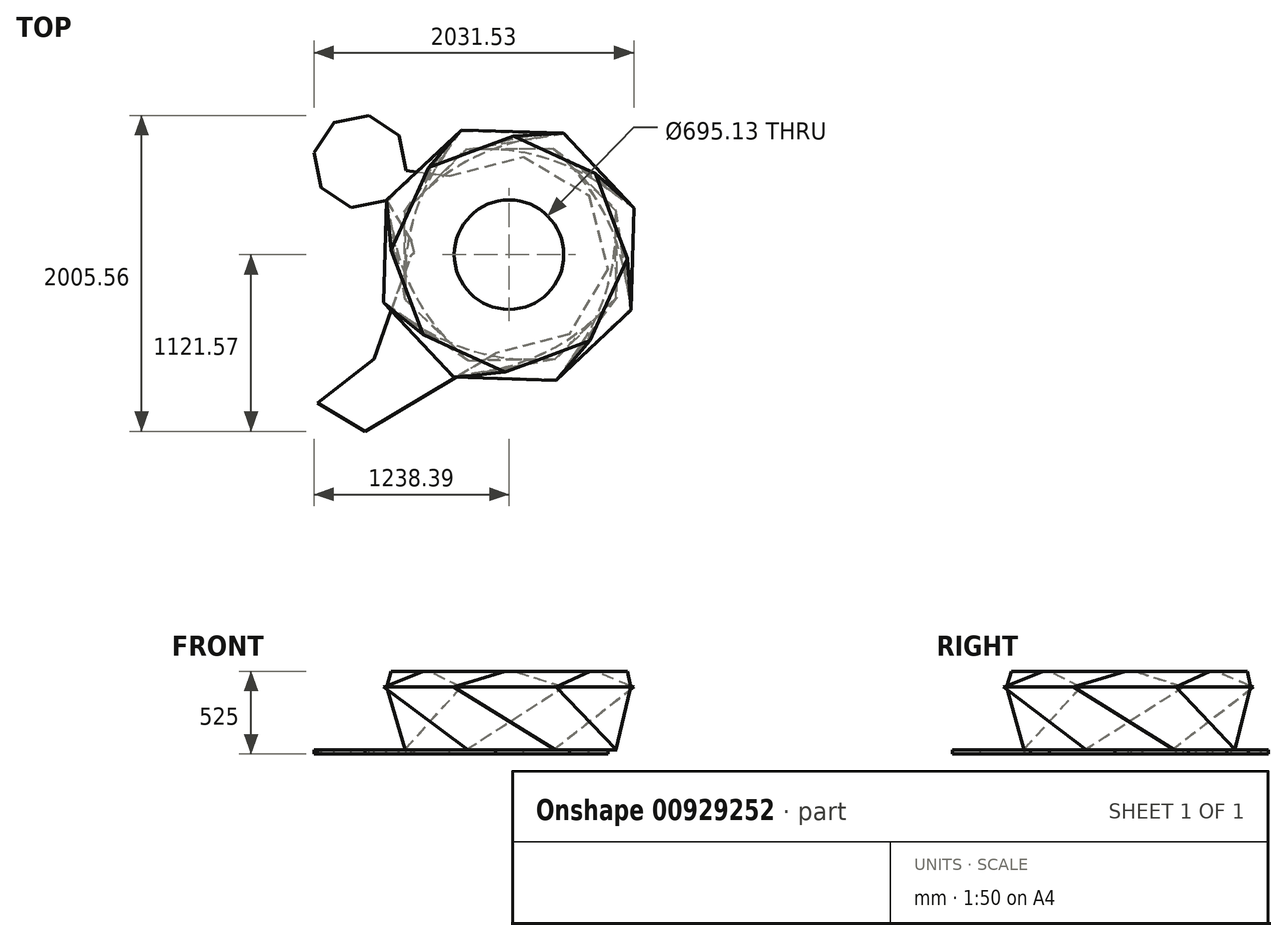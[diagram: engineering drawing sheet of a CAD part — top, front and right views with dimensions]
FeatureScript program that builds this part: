
annotation { "Feature Type Name" : "Feature", "Feature Type Description" : "" }
export const myFeature = defineFeature(function(context is Context, id is Id, definition is map)
    precondition{}
    {
        {
            var Q0;
            Q0=qCreatedBy(makeId("Top.planeOp"),FACE);
            var sketch = newSketch(context, id + "F0", { "sketchPlane" : qUnion([Q0])});
            skLineSegment(sketch, "E0", {"start": v(0, 0) * mm, "end": v(-1250, 0) * mm, "construction": true});
            skLineSegment(sketch, "E1", {"start": v(0, 0) * mm, "end": v(0, 1250) * mm, "construction": true});
            skLineSegment(sketch, "E2", {"start": v(0, 1250) * mm, "end": v(-1250, 0) * mm, "construction": true});
            skLineSegment(sketch, "E3.bottom", {"start": v(-1250, 0) * mm, "end": v(0, 0) * mm, "construction": true});
            skLineSegment(sketch, "E3.top", {"start": v(-1250, 1250) * mm, "end": v(0, 1250) * mm, "construction": true});
            skLineSegment(sketch, "E3.left", {"start": v(-1250, 0) * mm, "end": v(-1250, 1250) * mm, "construction": true});
            skLineSegment(sketch, "E4", {"start": v(-1250, 1250) * mm, "end": v(0, 0) * mm, "construction": true});
            skLineSegment(sketch, "E5", {"start": v(-625, 625) * mm, "end": v(0, 625) * mm, "construction": true});
            skLineSegment(sketch, "E6", {"start": v(0, 625) * mm, "end": v(-625, 625) * mm, "construction": true});
            skLineSegment(sketch, "E7", {"start": v(-625, 625) * mm, "end": v(-1250, 625) * mm, "construction": true});
            skLineSegment(sketch, "E8", {"start": v(-1250, 625) * mm, "end": v(-625, 625) * mm, "construction": true});
            skLineSegment(sketch, "E9", {"start": v(-625, 625) * mm, "end": v(-625, 1250) * mm, "construction": true});
            skLineSegment(sketch, "E10", {"start": v(-625, 625) * mm, "end": v(-625, 0) * mm, "construction": true});
            skCircle(sketch, "E11.cCircle", {"center": v(-625, 625) * mm, "radius": 583.1 * mm, "construction": true});
            skLineSegment(sketch, "E11.0", {"start": v(-1250, 712.8) * mm, "end": v(-1004.86, 1129.03) * mm});
            skLineSegment(sketch, "E11.1", {"start": v(-1004.86, 1129.03) * mm, "end": v(-537.2, 1250) * mm});
            skLineSegment(sketch, "E11.2", {"start": v(-537.2, 1250) * mm, "end": v(-120.97, 1004.86) * mm});
            skLineSegment(sketch, "E11.3", {"start": v(-120.97, 1004.86) * mm, "end": v(0, 537.2) * mm});
            skLineSegment(sketch, "E11.4", {"start": v(0, 537.2) * mm, "end": v(-245.14, 120.97) * mm});
            skLineSegment(sketch, "E11.5", {"start": v(-245.14, 120.97) * mm, "end": v(-712.8, 0) * mm});
            skLineSegment(sketch, "E11.6", {"start": v(-712.8, 0) * mm, "end": v(-1129.03, 245.14) * mm});
            skLineSegment(sketch, "E11.7", {"start": v(-1129.03, 245.14) * mm, "end": v(-1250, 712.8) * mm});
            skPoint(sketch, "E11.0.midPoint", {"position": v(-1127.43, 920.91) * mm});
            skLineSegment(sketch, "E12", {"start": v(-1127.43, 920.91) * mm, "end": v(-1574.38, 1218.8) * mm, "construction": true});
            skCircle(sketch, "E13.cCircle", {"center": v(-1574.38, 1218.8) * mm, "radius": 275.36 * mm, "construction": true});
            skLineSegment(sketch, "E13.0", {"start": v(-1632.18, 926.4) * mm, "end": v(-1822, 1052.9) * mm});
            skLineSegment(sketch, "E13.1", {"start": v(-1822, 1052.9) * mm, "end": v(-1866.78, 1276.6) * mm});
            skLineSegment(sketch, "E13.2", {"start": v(-1866.78, 1276.6) * mm, "end": v(-1740.27, 1466.42) * mm});
            skLineSegment(sketch, "E13.3", {"start": v(-1740.27, 1466.42) * mm, "end": v(-1516.58, 1511.19) * mm});
            skLineSegment(sketch, "E13.4", {"start": v(-1516.58, 1511.19) * mm, "end": v(-1326.76, 1384.67) * mm});
            skLineSegment(sketch, "E13.5", {"start": v(-1326.76, 1384.67) * mm, "end": v(-1281.99, 1161) * mm});
            skLineSegment(sketch, "E13.6", {"start": v(-1281.99, 1161) * mm, "end": v(-1408.5, 971.17) * mm});
            skLineSegment(sketch, "E13.7", {"start": v(-1408.5, 971.17) * mm, "end": v(-1632.18, 926.4) * mm});
            skPoint(sketch, "E13.0.midPoint", {"position": v(-1727.1, 989.65) * mm});
            skLineSegment(sketch, "E14", {"start": v(-1408.5, 971.17) * mm, "end": v(-1250, 712.8) * mm});
            skLineSegment(sketch, "E15", {"start": v(-1281.99, 1161) * mm, "end": v(-1004.86, 1129.03) * mm});
            skLineSegment(sketch, "E16", {"start": v(-1129.03, 245.14) * mm, "end": v(-1845.08, -315.8) * mm});
            skLineSegment(sketch, "E17", {"start": v(-1845.08, -315.8) * mm, "end": v(-1541.9, -494.37) * mm});
            skLineSegment(sketch, "E18", {"start": v(-1541.9, -494.37) * mm, "end": v(-712.8, 0) * mm});
            skLineSegment(sketch, "E19", {"start": v(-1487.05, -35.33) * mm, "end": v(-1250, 625) * mm});
            skLineSegment(sketch, "E20", {"start": v(-1250, 625) * mm, "end": v(-1231.96, 643.04) * mm});
            skSolve(sketch);
        }
        {
            var Q0;
            Q0=makeQuery(id+"F0.imprint","IMPRINT",FACE,{"disambiguationData":[TD([[makeQuery(id+"F0.imprint","IMPRINT",EDGE,{"derivedFrom":sQuery(id+"F0.wireOp",EDGE,"E13.0")}),-1.0]])]});
            var Q1;
            Q1=makeQuery(id+"F0.imprint","IMPRINT",FACE,{"disambiguationData":[TD([[makeQuery(id+"F0.imprint","IMPRINT",EDGE,{"derivedFrom":sQuery(id+"F0.wireOp",EDGE,"E11.0")}),1.0]])]});
            var Q2;
            {var subQ0=sQuery(id+"F0.wireOp",EDGE,"E11.0");Q2=makeQuery(id+"F0.imprint","IMPRINT",FACE,{"disambiguationData":[TD([[makeQuery(id+"F0.imprint","IMPRINT",EDGE,{"derivedFrom":subQ0}),-1.0]])]});}
            var Q3;
            {var subQ4=sQuery(id+"F0.wireOp",EDGE,"E19");Q3=makeQuery(id+"F0.imprint","IMPRINT",FACE,{"disambiguationData":[TD([[makeQuery(id+"F0.imprint","IMPRINT",EDGE,{"derivedFrom":subQ4}),-1.0]])]});}
            var Q4;
            {var subQ3=sQuery(id+"F0.wireOp",EDGE,"E11.6");Q4=makeQuery(id+"F0.imprint","IMPRINT",FACE,{"disambiguationData":[TD([[makeQuery(id+"F0.imprint","IMPRINT",EDGE,{"derivedFrom":subQ3}),1.0]])]});}
            extrude(context, id + "F1", {"entities" : qUnion([Q0, Q1, Q2, Q3, Q4]), "oppositeDirection" : true, "depth" : 25 * mm, "offsetDistance" : 25 * mm});
        }
        {
            var Q0;
            Q0=qCreatedBy(makeId("Top.planeOp"),FACE);
            cPlane(context, id + "F2", {"entities" : qUnion([Q0]), "cplaneType" : CPlaneType.OFFSET, "offset" : 100 * mm, "width" : 150 * mm, "height" : 150 * mm});
        }
        {
            var Q0;
            Q0=qCreatedBy(makeId("Top.planeOp"),FACE);
            var sketch = newSketch(context, id + "F3", { "sketchPlane" : qUnion([Q0])});
            skCircle(sketch, "E21.cCircle", {"center": v(-619.06, 628.41) * mm, "radius": 671.72 * mm, "construction": true});
            skLineSegment(sketch, "E21.0", {"start": v(-1294.06, 898.6) * mm, "end": v(-905.3, 1296.76) * mm});
            skLineSegment(sketch, "E21.1", {"start": v(-905.3, 1296.76) * mm, "end": v(-348.87, 1303.41) * mm});
            skLineSegment(sketch, "E21.2", {"start": v(-348.87, 1303.41) * mm, "end": v(49.29, 914.66) * mm});
            skLineSegment(sketch, "E21.3", {"start": v(49.29, 914.66) * mm, "end": v(55.94, 358.22) * mm});
            skLineSegment(sketch, "E21.4", {"start": v(55.94, 358.22) * mm, "end": v(-332.82, -39.94) * mm});
            skLineSegment(sketch, "E21.5", {"start": v(-332.82, -39.94) * mm, "end": v(-889.25, -46.59) * mm});
            skLineSegment(sketch, "E21.6", {"start": v(-889.25, -46.59) * mm, "end": v(-1287.41, 342.17) * mm});
            skLineSegment(sketch, "E21.7", {"start": v(-1287.41, 342.17) * mm, "end": v(-1294.06, 898.6) * mm});
            skPoint(sketch, "E21.0.midPoint", {"position": v(-1099.68, 1097.68) * mm});
            skSolve(sketch);
        }
        {
            var Q0;
            Q0=qCreatedBy(makeId("Top.planeOp"),FACE);
            cPlane(context, id + "F4", {"entities" : qUnion([Q0]), "cplaneType" : CPlaneType.OFFSET, "offset" : 200 * mm, "width" : 150 * mm, "height" : 150 * mm});
        }
        {
            var Q0;
            Q0=qCreatedBy(makeId("Top.planeOp"),FACE);
            cPlane(context, id + "F5", {"entities" : qUnion([Q0]), "cplaneType" : CPlaneType.OFFSET, "offset" : 400 * mm, "width" : 150 * mm, "height" : 150 * mm});
        }
        {
            var Q0;
            Q0=qCreatedBy(id+"F5.planeOp",FACE);
            var sketch = newSketch(context, id + "F6", { "sketchPlane" : qUnion([Q0])});
            skCircle(sketch, "E22.cCircle", {"center": v(-630.1, 623.79) * mm, "radius": 785.3 * mm, "construction": true});
            skLineSegment(sketch, "E22.0", {"start": v(-1424.97, 322.63) * mm, "end": v(-1405.1, 972.9) * mm});
            skLineSegment(sketch, "E22.1", {"start": v(-1405.1, 972.9) * mm, "end": v(-931.26, 1418.65) * mm});
            skLineSegment(sketch, "E22.2", {"start": v(-931.26, 1418.65) * mm, "end": v(-281, 1398.79) * mm});
            skLineSegment(sketch, "E22.3", {"start": v(-281, 1398.79) * mm, "end": v(164.75, 924.94) * mm});
            skLineSegment(sketch, "E22.4", {"start": v(164.75, 924.94) * mm, "end": v(144.9, 274.68) * mm});
            skLineSegment(sketch, "E22.5", {"start": v(144.9, 274.68) * mm, "end": v(-328.96, -171.08) * mm});
            skLineSegment(sketch, "E22.6", {"start": v(-328.96, -171.08) * mm, "end": v(-979.22, -151.21) * mm});
            skLineSegment(sketch, "E22.7", {"start": v(-979.22, -151.21) * mm, "end": v(-1424.97, 322.63) * mm});
            skPoint(sketch, "E22.0.midPoint", {"position": v(-1415.04, 647.76) * mm});
            skSolve(sketch);
        }
        {
            var Q0;
            Q0=qCreatedBy(id+"F5.planeOp",FACE);
            cPlane(context, id + "F7", {"entities" : qUnion([Q0]), "cplaneType" : CPlaneType.OFFSET, "offset" : 100 * mm, "width" : 150 * mm, "height" : 150 * mm});
        }
        {
            var Q0;
            Q0=qCreatedBy(id+"F7.planeOp",FACE);
            var sketch = newSketch(context, id + "F8", { "sketchPlane" : qUnion([Q0])});
            skPoint(sketch, "E23.0.midPoint", {"position": v(-1069.33, 0) * mm});
            skCircle(sketch, "E24.cCircle", {"center": v(-626.9, 630.44) * mm, "radius": 692.9 * mm, "construction": true});
            skLineSegment(sketch, "E24.0", {"start": v(-653.28, -119.1) * mm, "end": v(-1175.56, 119.1) * mm});
            skLineSegment(sketch, "E24.1", {"start": v(-1175.56, 119.1) * mm, "end": v(-1376.44, 656.82) * mm});
            skLineSegment(sketch, "E24.2", {"start": v(-1376.44, 656.82) * mm, "end": v(-1138.26, 1179.1) * mm});
            skLineSegment(sketch, "E24.3", {"start": v(-1138.26, 1179.1) * mm, "end": v(-600.53, 1379.98) * mm});
            skLineSegment(sketch, "E24.4", {"start": v(-600.53, 1379.98) * mm, "end": v(-78.26, 1141.8) * mm});
            skLineSegment(sketch, "E24.5", {"start": v(-78.26, 1141.8) * mm, "end": v(122.63, 604.07) * mm});
            skLineSegment(sketch, "E24.6", {"start": v(122.63, 604.07) * mm, "end": v(-115.55, 81.8) * mm});
            skLineSegment(sketch, "E24.7", {"start": v(-115.55, 81.8) * mm, "end": v(-653.28, -119.1) * mm});
            skPoint(sketch, "E24.0.midPoint", {"position": v(-914.42, 0) * mm});
            skSolve(sketch);
        }
        {
            var Q1;
            Q1 = qSketchRegion(id + "F3", true);
            var Q2;
            Q2=makeQuery(id+"F6.imprint","IMPRINT",FACE,{"disambiguationData":[TD([[makeQuery(id+"F6.imprint","IMPRINT",EDGE,{"derivedFrom":sQuery(id+"F6.wireOp",EDGE,"E22.0")}),-1.0]])]});
            var Q3;
            Q3=sQuery(id+"F3.wireOp",VERTEX,"E21.6.end");
            var Q4;
            Q4=sQuery(id+"F6.wireOp",VERTEX,"E22.0.end");
            loft(context, id + "F9", {"operationType" : NewBodyOperationType.ADD, "sheetProfilesArray" : [{ "sheetProfileEntities" : qUnion([Q1]) }, { "sheetProfileEntities" : qUnion([Q2]) }], "matchConnections" : true, "connections" : [{ "connectionEntities" : qUnion([Q3, Q4]), "connectionEdgeQueries" : qUnion([]), "connectionEdgeParameters" : [] }]});
        }
        {
            var Q1;
            Q1 = qSketchRegion(id + "F6", true);
            var Q2;
            Q2 = qSketchRegion(id + "F8", true);
            var Q3;
            Q3=sQuery(id+"F6.wireOp",VERTEX,"E22.1.end");
            var Q4;
            Q4=sQuery(id+"F8.wireOp",VERTEX,"E24.2.end");
            loft(context, id + "F10", {"operationType" : NewBodyOperationType.ADD, "sheetProfilesArray" : [{ "sheetProfileEntities" : qUnion([Q1]) }, { "sheetProfileEntities" : qUnion([Q2]) }], "matchConnections" : true, "connections" : [{ "connectionEntities" : qUnion([Q3, Q4]), "connectionEdgeQueries" : qUnion([]), "connectionEdgeParameters" : [] }]});
        }
        {
            var Q0;
            Q0=makeQuery(id+"F10.opLoft","CAP_FACE",FACE,{"disambiguationData":[OSD([makeQuery(id+"F8.imprint","IMPRINT",FACE,{"disambiguationData":[TD([[makeQuery(id+"F8.imprint","IMPRINT",EDGE,{"derivedFrom":sQuery(id+"F8.wireOp",EDGE,"E24.0")}),-1.0]])]})])],"isStart":true});
            var Q1;
            Q1=makeQuery(id+"F1.opExtrude","SWEPT_BODY",BODY,{"disambiguationData":[OSD([sQuery(id+"F0.wireOp",EDGE,"E11.1"),sQuery(id+"F0.wireOp",EDGE,"E11.2"),sQuery(id+"F0.wireOp",EDGE,"E11.3"),sQuery(id+"F0.wireOp",EDGE,"E11.4"),sQuery(id+"F0.wireOp",EDGE,"E11.5"),sQuery(id+"F0.wireOp",EDGE,"E11.7"),sQuery(id+"F0.wireOp",EDGE,"E13.0"),sQuery(id+"F0.wireOp",EDGE,"E13.1"),sQuery(id+"F0.wireOp",EDGE,"E13.2"),sQuery(id+"F0.wireOp",EDGE,"E13.3"),sQuery(id+"F0.wireOp",EDGE,"E13.4"),sQuery(id+"F0.wireOp",EDGE,"E13.5"),sQuery(id+"F0.wireOp",EDGE,"E13.7"),sQuery(id+"F0.wireOp",EDGE,"E14"),sQuery(id+"F0.wireOp",EDGE,"E15"),sQuery(id+"F0.wireOp",EDGE,"E16"),sQuery(id+"F0.wireOp",EDGE,"E17"),sQuery(id+"F0.wireOp",EDGE,"E18"),sQuery(id+"F0.wireOp",EDGE,"E19"),sQuery(id+"F0.wireOp",EDGE,"E20")])]});
            shell(context, id + "F11", {"isHollow" : true, "entities" : qUnion([Q0]), "parts" : qUnion([Q1]), "thickness" : 2.5 * mm});
        }
        {
            var Q0;
            Q0=makeQuery(id+"F10.opLoft","CAP_FACE",FACE,{"disambiguationData":[OSD([makeQuery(id+"F8.imprint","IMPRINT",FACE,{"disambiguationData":[TD([[makeQuery(id+"F8.imprint","IMPRINT",EDGE,{"derivedFrom":sQuery(id+"F8.wireOp",EDGE,"E24.0")}),-1.0]])]})])],"isStart":true});
            var sketch = newSketch(context, id + "F12", { "sketchPlane" : qUnion([Q0])});
            skLineSegment(sketch, "E25", {"start": v(-1389.95, 627.2) * mm, "end": v(133.18, 627.2) * mm, "construction": true});
            skLineSegment(sketch, "E26", {"start": v(-1389.95, 627.2) * mm, "end": v(-975.95, 627.2) * mm});
            skLineSegment(sketch, "E27", {"start": v(-628.39, 627.2) * mm, "end": v(-628.39, 826.4) * mm, "construction": true});
            skLineSegment(sketch, "E28", {"start": v(133.18, 627.2) * mm, "end": v(-280.82, 627.2) * mm});
            skCircle(sketch, "E29", {"center": v(-628.39, 627.2) * mm, "radius": 347.56 * mm});
            skSolve(sketch);
        }
        {
            var Q0;
            Q0 = qSketchRegion(id + "F12", true);
            extrude(context, id + "F13", {"entities" : qUnion([Q0]), "operationType" : NewBodyOperationType.REMOVE, "oppositeDirection" : true, "depth" : 100 * mm, "offsetDistance" : 25 * mm});
        }
    });
